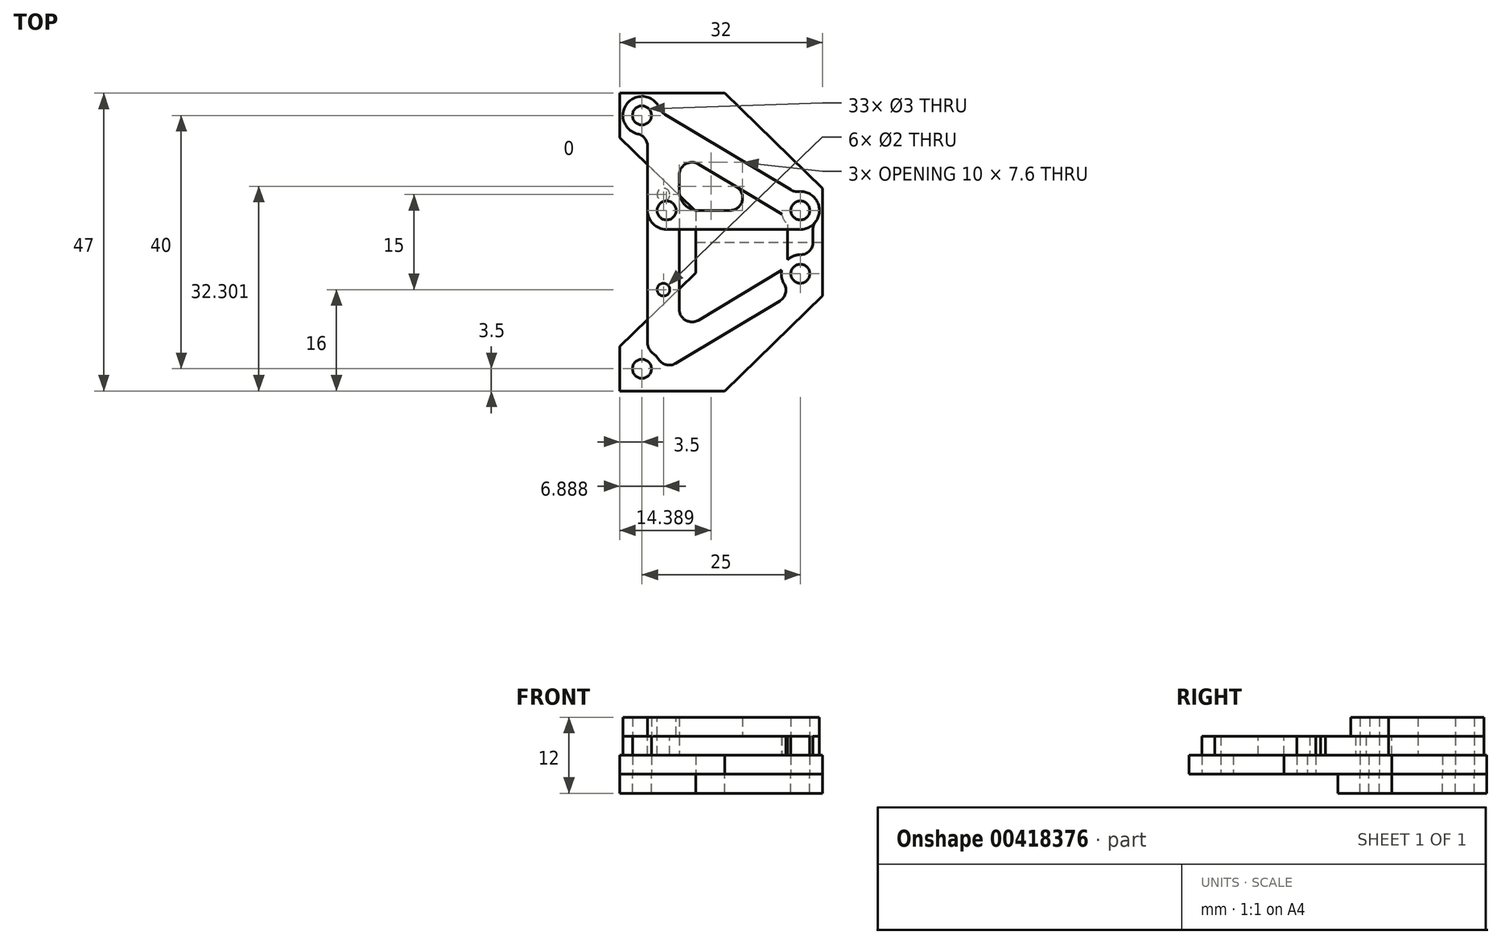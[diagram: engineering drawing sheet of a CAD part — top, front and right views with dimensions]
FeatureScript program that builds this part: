
annotation { "Feature Type Name" : "Feature", "Feature Type Description" : "" }
export const myFeature = defineFeature(function(context is Context, id is Id, definition is map)
    precondition{}
    {
        {
            var Q0;
            Q0=qCreatedBy(makeId("Top.planeOp"),FACE);
            var sketch = newSketch(context, id + "F0", { "sketchPlane" : qUnion([Q0])});
            skCircle(sketch, "E0", {"center": v(0, 20) * mm, "radius": 1.5 * mm});
            skCircle(sketch, "E1", {"center": v(25, 5) * mm, "radius": 1.5 * mm});
            skCircle(sketch, "E2.MirrorC", {"center": v(0, -20) * mm, "radius": 1.5 * mm});
            skCircle(sketch, "E3.MirrorC", {"center": v(25, -5) * mm, "radius": 1.5 * mm});
            skLineSegment(sketch, "E4", {"start": v(8.5, 4.85) * mm, "end": v(-3.5, 16.5) * mm});
            skLineSegment(sketch, "E5", {"start": v(-3.5, 16.5) * mm, "end": v(-3.5, 23.5) * mm});
            skLineSegment(sketch, "E6", {"start": v(-3.5, 23.5) * mm, "end": v(13.05, 23.5) * mm});
            skLineSegment(sketch, "E7", {"start": v(13.05, 23.5) * mm, "end": v(28.5, 8.5) * mm});
            skLineSegment(sketch, "E8", {"start": v(28.5, 8.5) * mm, "end": v(28.5, 0) * mm});
            skLineSegment(sketch, "E9.MirrorCS", {"start": v(8.5, -4.85) * mm, "end": v(-3.5, -16.5) * mm});
            skLineSegment(sketch, "E10.MirrorCS", {"start": v(-3.5, -16.5) * mm, "end": v(-3.5, -23.5) * mm});
            skLineSegment(sketch, "E11.MirrorCS", {"start": v(-3.5, -23.5) * mm, "end": v(13.05, -23.5) * mm});
            skLineSegment(sketch, "E12.MirrorCS", {"start": v(13.05, -23.5) * mm, "end": v(28.5, -8.5) * mm});
            skLineSegment(sketch, "E13.MirrorCS", {"start": v(28.5, -8.5) * mm, "end": v(28.5, 0) * mm});
            skLineSegment(sketch, "E14", {"start": v(8.5, 4.85) * mm, "end": v(8.5, -4.85) * mm});
            skPoint(sketch, "E15.orphan", {"position": v(13.5, 0) * mm});
            skLineSegment(sketch, "E16", {"start": v(8.5, 0) * mm, "end": v(28.5, 0) * mm});
            skSolve(sketch);
        }
        {
            var Q0;
            Q0 = qSketchRegion(id + "F0", true);
            extrude(context, id + "F1", {"entities" : qUnion([Q0]), "depth" : 3 * mm, "offsetDistance" : 25 * mm});
        }
        {
            var Q0;
            Q0=makeQuery(id+"F0.imprint","IMPRINT",FACE,{"disambiguationData":[TD([[makeQuery(id+"F0.imprint","IMPRINT",EDGE,{"derivedFrom":sQuery(id+"F0.wireOp",EDGE,"E0")}),-1.0]])]});
            extrude(context, id + "F2", {"entities" : qUnion([Q0]), "oppositeDirection" : true, "depth" : 3 * mm, "offsetDistance" : 25 * mm});
        }
        {
            var Q0;
            Q0=makeQuery(id+"F1.opExtrude","CAP_FACE",FACE,{"disambiguationData":[OSD([sQuery(id+"F0.wireOp",EDGE,"E0"),sQuery(id+"F0.wireOp",EDGE,"E1"),sQuery(id+"F0.wireOp",EDGE,"E2.MirrorC"),sQuery(id+"F0.wireOp",EDGE,"E3.MirrorC"),sQuery(id+"F0.wireOp",EDGE,"E4"),sQuery(id+"F0.wireOp",EDGE,"E5"),sQuery(id+"F0.wireOp",EDGE,"E6"),sQuery(id+"F0.wireOp",EDGE,"E7"),sQuery(id+"F0.wireOp",EDGE,"E8"),sQuery(id+"F0.wireOp",EDGE,"E9.MirrorCS"),sQuery(id+"F0.wireOp",EDGE,"E10.MirrorCS"),sQuery(id+"F0.wireOp",EDGE,"E11.MirrorCS"),sQuery(id+"F0.wireOp",EDGE,"E12.MirrorCS"),sQuery(id+"F0.wireOp",EDGE,"E13.MirrorCS"),sQuery(id+"F0.wireOp",EDGE,"E14")])],"isStart":false});
            var sketch = newSketch(context, id + "F3", { "sketchPlane" : qUnion([Q0])});
            skCircle(sketch, "E17.0", {"center": v(0, 20) * mm, "radius": 1.5 * mm});
            skCircle(sketch, "E18.0", {"center": v(25, 5) * mm, "radius": 1.5 * mm});
            skCircle(sketch, "E19", {"center": v(0, 20) * mm, "radius": 3 * mm});
            skCircle(sketch, "E20", {"center": v(25, 5) * mm, "radius": 3 * mm});
            skPoint(sketch, "E21", {"position": v(1.5, 20) * mm});
            skPoint(sketch, "E22", {"position": v(3, 20) * mm});
            skPoint(sketch, "E23", {"position": v(26.5, 5) * mm});
            skPoint(sketch, "E24", {"position": v(28, 5) * mm});
            skLineSegment(sketch, "E25", {"start": v(0, 20) * mm, "end": v(25, 5) * mm, "construction": true});
            skCircle(sketch, "E26.0", {"center": v(25, -5) * mm, "radius": 1.5 * mm});
            skLineSegment(sketch, "E27", {"start": v(25, 5) * mm, "end": v(25, -5) * mm, "construction": true});
            skCircle(sketch, "E28.MirrorC", {"center": v(25, -5) * mm, "radius": 3 * mm});
            skCircle(sketch, "E29.MirrorC", {"center": v(0, -20) * mm, "radius": 3 * mm});
            skLineSegment(sketch, "E30", {"start": v(23, 2.76) * mm, "end": v(23, -2.76) * mm});
            skLineSegment(sketch, "E31.MirrorCS", {"start": v(27, 2.76) * mm, "end": v(27, -2.76) * mm});
            skLineSegment(sketch, "E32", {"start": v(0.89, 17.13) * mm, "end": v(22.05, 4.44) * mm});
            skLineSegment(sketch, "E33.MirrorCS", {"start": v(2.95, 20.56) * mm, "end": v(24.11, 7.87) * mm});
            skLineSegment(sketch, "E34.MirrorCS", {"start": v(0.89, -17.13) * mm, "end": v(22.05, -4.44) * mm});
            skLineSegment(sketch, "E35.MirrorCS", {"start": v(2.95, -20.56) * mm, "end": v(24.11, -7.87) * mm});
            skLineSegment(sketch, "E36", {"start": v(0.89, 17.13) * mm, "end": v(0.89, -17.13) * mm});
            skLineSegment(sketch, "E37", {"start": v(5.89, 14.13) * mm, "end": v(5.89, -14.13) * mm});
            skSolve(sketch);
        }
        {
            var Q0;
            Q0=makeQuery(id+"F3.imprint","IMPRINT",FACE,{"disambiguationData":[TD([[makeQuery(id+"F3.imprint","IMPRINT",EDGE,{"derivedFrom":sQuery(id+"F3.wireOp",EDGE,"E17.0")}),-1.0]])]});
            var Q1;
            Q1=makeQuery(id+"F3.imprint","IMPRINT",FACE,{"disambiguationData":[TD([[makeQuery(id+"F3.imprint","IMPRINT",EDGE,{"derivedFrom":makeQuery(id+"F1.opExtrude","CAP_EDGE",EDGE,{"disambiguationData":[OSD([sQuery(id+"F0.wireOp",EDGE,"E2.MirrorC")])],"isStart":false})}),1.0]])]});
            var Q2;
            {var subQ0=sQuery(id+"F3.wireOp",EDGE,"E30");Q2=makeQuery(id+"F3.imprint","IMPRINT",FACE,{"disambiguationData":[TD([[makeQuery(id+"F3.imprint","IMPRINT",EDGE,{"derivedFrom":subQ0}),1.0]])]});}
            var Q3;
            Q3=makeQuery(id+"F3.imprint","IMPRINT",FACE,{"disambiguationData":[TD([[makeQuery(id+"F3.imprint","IMPRINT",EDGE,{"derivedFrom":sQuery(id+"F3.wireOp",EDGE,"E18.0")}),-1.0]])]});
            var Q4;
            {var subQ6=sQuery(id+"F3.wireOp",EDGE,"E33.MirrorCS");Q4=makeQuery(id+"F3.imprint","IMPRINT",FACE,{"disambiguationData":[TD([[makeQuery(id+"F3.imprint","IMPRINT",EDGE,{"derivedFrom":subQ6}),-1.0]])]});}
            var Q5;
            Q5=makeQuery(id+"F3.imprint","IMPRINT",FACE,{"disambiguationData":[TD([[makeQuery(id+"F3.imprint","IMPRINT",EDGE,{"derivedFrom":sQuery(id+"F3.wireOp",EDGE,"E26.0")}),1.0]])]});
            var Q6;
            {var subQ6=sQuery(id+"F3.wireOp",EDGE,"E35.MirrorCS");Q6=makeQuery(id+"F3.imprint","IMPRINT",FACE,{"disambiguationData":[TD([[makeQuery(id+"F3.imprint","IMPRINT",EDGE,{"derivedFrom":subQ6}),1.0]])]});}
            var Q7;
            {var subQ1=sQuery(id+"F3.wireOp",EDGE,"E32");var subQ3=sQuery(id+"F3.wireOp",EDGE,"E37");var subQ4=makeQuery(id+"F3.imprint","INTERSECT",VERTEX,{"derivedFrom":[subQ1,subQ3]});Q7=makeQuery(id+"F3.imprint","IMPRINT",FACE,{"disambiguationData":[TD([[makeQuery(id+"F3.imprint","IMPRINT",EDGE,{"disambiguationData":[TD([[subQ4,-1.0]])],"derivedFrom":subQ3}),-1.0]])]});}
            var Q8;
            {var subQ1=sQuery(id+"F3.wireOp",EDGE,"E34.MirrorCS");var subQ3=sQuery(id+"F3.wireOp",EDGE,"E37");var subQ4=makeQuery(id+"F3.imprint","INTERSECT",VERTEX,{"derivedFrom":[subQ1,subQ3]});Q8=makeQuery(id+"F3.imprint","IMPRINT",FACE,{"disambiguationData":[TD([[makeQuery(id+"F3.imprint","IMPRINT",EDGE,{"disambiguationData":[TD([[subQ4,1.0]])],"derivedFrom":subQ3}),-1.0]])]});}
            var Q9;
            {var subQ0=sQuery(id+"F3.wireOp",EDGE,"E36");var subQ1=makeQuery(id+"F1.opExtrude","CAP_EDGE",EDGE,{"disambiguationData":[OSD([sQuery(id+"F0.wireOp",EDGE,"E4")])],"isStart":false});var subQ2=makeQuery(id+"F3.imprint","INTERSECT",VERTEX,{"derivedFrom":[subQ1,subQ0]});Q9=makeQuery(id+"F3.imprint","IMPRINT",FACE,{"disambiguationData":[TD([[makeQuery(id+"F3.imprint","IMPRINT",EDGE,{"disambiguationData":[TD([[subQ2,-1.0]])],"derivedFrom":subQ0}),1.0]])]});}
            extrude(context, id + "F4", {"entities" : qUnion([Q0, Q1, Q2, Q3, Q4, Q5, Q6, Q7, Q8, Q9]), "depth" : 3 * mm, "offsetDistance" : 25 * mm});
        }
        {
            var Q0;
            Q0=makeQuery(id+"F4.opExtrude","SWEPT_EDGE",EDGE,{"disambiguationData":[OSD([sQuery(id+"F3.wireOp",EDGE,"E19"),sQuery(id+"F3.wireOp",EDGE,"E32"),sQuery(id+"F3.wireOp",EDGE,"E36")])]});
            var Q1;
            Q1=makeQuery(id+"F4.opExtrude","SWEPT_EDGE",EDGE,{"disambiguationData":[OSD([sQuery(id+"F3.wireOp",EDGE,"E29.MirrorC"),sQuery(id+"F3.wireOp",EDGE,"E34.MirrorCS"),sQuery(id+"F3.wireOp",EDGE,"E36")])]});
            var Q2;
            Q2=makeQuery(id+"F4.opExtrude","SWEPT_EDGE",EDGE,{"disambiguationData":[OSD([sQuery(id+"F3.wireOp",EDGE,"E29.MirrorC"),sQuery(id+"F3.wireOp",EDGE,"E35.MirrorCS")])]});
            var Q3;
            Q3=makeQuery(id+"F4.opExtrude","SWEPT_EDGE",EDGE,{"disambiguationData":[OSD([sQuery(id+"F3.wireOp",EDGE,"E28.MirrorC"),sQuery(id+"F3.wireOp",EDGE,"E35.MirrorCS")])]});
            var Q4;
            Q4=makeQuery(id+"F4.opExtrude","SWEPT_EDGE",EDGE,{"disambiguationData":[OSD([sQuery(id+"F3.wireOp",EDGE,"E20"),sQuery(id+"F3.wireOp",EDGE,"E31.MirrorCS")])]});
            var Q5;
            Q5=makeQuery(id+"F4.opExtrude","SWEPT_EDGE",EDGE,{"disambiguationData":[OSD([sQuery(id+"F3.wireOp",EDGE,"E28.MirrorC"),sQuery(id+"F3.wireOp",EDGE,"E31.MirrorCS")])]});
            var Q6;
            Q6=makeQuery(id+"F4.opExtrude","SWEPT_EDGE",EDGE,{"disambiguationData":[OSD([sQuery(id+"F3.wireOp",EDGE,"E20"),sQuery(id+"F3.wireOp",EDGE,"E33.MirrorCS")])]});
            var Q7;
            Q7=makeQuery(id+"F4.opExtrude","SWEPT_EDGE",EDGE,{"disambiguationData":[OSD([sQuery(id+"F3.wireOp",EDGE,"E34.MirrorCS"),sQuery(id+"F3.wireOp",EDGE,"E37")])]});
            var Q8;
            Q8=makeQuery(id+"F4.opExtrude","SWEPT_EDGE",EDGE,{"disambiguationData":[OSD([sQuery(id+"F3.wireOp",EDGE,"E32"),sQuery(id+"F3.wireOp",EDGE,"E37")])]});
            var Q9;
            Q9=makeQuery(id+"F4.opExtrude","SWEPT_EDGE",EDGE,{"disambiguationData":[OSD([sQuery(id+"F3.wireOp",EDGE,"E19"),sQuery(id+"F3.wireOp",EDGE,"E33.MirrorCS")])]});
            fillet(context, id + "F5", {"entities" : qUnion([Q0, Q1, Q2, Q3, Q4, Q5, Q6, Q7, Q8, Q9]), "radius" : 2 * mm, "tangentPropagation" : true, "allowEdgeOverflow" : false});
        }
        {
            var Q0;
            Q0=makeQuery(id+"F4.opExtrude","CAP_FACE",FACE,{"disambiguationData":[OSD([sQuery(id+"F0.wireOp",EDGE,"E2.MirrorC"),sQuery(id+"F3.wireOp",EDGE,"E17.0"),sQuery(id+"F3.wireOp",EDGE,"E18.0"),sQuery(id+"F3.wireOp",EDGE,"E19"),sQuery(id+"F3.wireOp",EDGE,"E20"),sQuery(id+"F3.wireOp",EDGE,"E26.0"),sQuery(id+"F3.wireOp",EDGE,"E28.MirrorC"),sQuery(id+"F3.wireOp",EDGE,"E29.MirrorC"),sQuery(id+"F3.wireOp",EDGE,"E30"),sQuery(id+"F3.wireOp",EDGE,"E31.MirrorCS"),sQuery(id+"F3.wireOp",EDGE,"E32"),sQuery(id+"F3.wireOp",EDGE,"E33.MirrorCS"),sQuery(id+"F3.wireOp",EDGE,"E34.MirrorCS"),sQuery(id+"F3.wireOp",EDGE,"E35.MirrorCS"),sQuery(id+"F3.wireOp",EDGE,"E36"),sQuery(id+"F3.wireOp",EDGE,"E37")])],"isStart":false});
            var sketch = newSketch(context, id + "F6", { "sketchPlane" : qUnion([Q0])});
            skCircle(sketch, "E38.0", {"center": v(0, 20) * mm, "radius": 3 * mm});
            skCircle(sketch, "E39.0", {"center": v(0, 20) * mm, "radius": 1.5 * mm});
            skCircle(sketch, "E40.0", {"center": v(25, 5) * mm, "radius": 1.5 * mm});
            skCircle(sketch, "E41.0", {"center": v(25, 5) * mm, "radius": 3 * mm});
            skArc(sketch, "E42.0", {"start": v(3.6, 20.17) * mm, "mid": v(3.11, 20.58) * mm, "end": v(2.78, 21.13) * mm});
            skLineSegment(sketch, "E43.0", {"start": v(2.95, 20.56) * mm, "end": v(24.11, 7.87) * mm});
            skArc(sketch, "E44.0", {"start": v(24.7, 7.98) * mm, "mid": v(24.05, 8.02) * mm, "end": v(23.46, 8.26) * mm});
            skArc(sketch, "E45.0", {"start": v(-0.67, 17.08) * mm, "mid": v(0.45, 16.37) * mm, "end": v(0.89, 15.13) * mm});
            skLineSegment(sketch, "E46.0", {"start": v(0.89, 17.13) * mm, "end": v(0.89, 2) * mm});
            skArc(sketch, "E47.0", {"start": v(5.89, 10.6) * mm, "mid": v(6.9, 12.34) * mm, "end": v(8.92, 12.32) * mm});
            skLineSegment(sketch, "E48.0", {"start": v(5.89, 14.13) * mm, "end": v(5.89, 2) * mm});
            skLineSegment(sketch, "E49.0", {"start": v(0.89, 17.13) * mm, "end": v(14.92, 8.71) * mm});
            skLineSegment(sketch, "E50", {"start": v(25, 2) * mm, "end": v(5.89, 2) * mm});
            skLineSegment(sketch, "E51", {"start": v(5.89, 5) * mm, "end": v(13.9, 5) * mm});
            skLineSegment(sketch, "E52", {"start": v(5.89, 2) * mm, "end": v(0.89, 2) * mm});
            skPoint(sketch, "E53.orphan", {"position": v(0.89, -17.13) * mm});
            skPoint(sketch, "E54.orphan", {"position": v(5.89, -14.13) * mm});
            skPoint(sketch, "E55.newPointA", {"position": v(22.05, 4.44) * mm});
            skArc(sketch, "E55.filletArc", {"start": v(13.9, 5) * mm, "mid": v(15.82, 6.47) * mm, "end": v(14.92, 8.71) * mm});
            skSolve(sketch);
        }
        {
            var Q0;
            Q0 = qSketchRegion(id + "F6", true);
            var Q1;
            {var subQ0=sQuery(id+"F6.wireOp",EDGE,"E47.0");Q1=makeQuery(id+"F6.imprint","IMPRINT",FACE,{"disambiguationData":[TD([[makeQuery(id+"F6.imprint","IMPRINT",EDGE,{"derivedFrom":subQ0}),1.0]])]});}
            extrude(context, id + "F7", {"entities" : qUnion([Q0, Q1]), "depth" : 3 * mm, "offsetDistance" : 25 * mm});
        }
        {
            var Q0;
            Q0=makeQuery(id+"F7.opExtrude","SWEPT_EDGE",EDGE,{"disambiguationData":[OSD([sQuery(id+"F6.wireOp",EDGE,"E48.0"),sQuery(id+"F6.wireOp",EDGE,"E51")])]});
            var Q1;
            Q1=makeQuery(id+"F7.opExtrude","SWEPT_EDGE",EDGE,{"disambiguationData":[OSD([sQuery(id+"F3.wireOp",EDGE,"E36"),sQuery(id+"F6.wireOp",EDGE,"E46.0"),sQuery(id+"F6.wireOp",EDGE,"E52")])]});
            fillet(context, id + "F8", {"entities" : qUnion([Q0, Q1]), "radius" : 3 * mm, "tangentPropagation" : true, "allowEdgeOverflow" : false});
        }
        {
            var Q0;
            Q0=makeQuery(id+"F4.opExtrude","CAP_FACE",FACE,{"disambiguationData":[OSD([sQuery(id+"F0.wireOp",EDGE,"E2.MirrorC"),sQuery(id+"F3.wireOp",EDGE,"E17.0"),sQuery(id+"F3.wireOp",EDGE,"E18.0"),sQuery(id+"F3.wireOp",EDGE,"E19"),sQuery(id+"F3.wireOp",EDGE,"E20"),sQuery(id+"F3.wireOp",EDGE,"E26.0"),sQuery(id+"F3.wireOp",EDGE,"E28.MirrorC"),sQuery(id+"F3.wireOp",EDGE,"E29.MirrorC"),sQuery(id+"F3.wireOp",EDGE,"E30"),sQuery(id+"F3.wireOp",EDGE,"E31.MirrorCS"),sQuery(id+"F3.wireOp",EDGE,"E32"),sQuery(id+"F3.wireOp",EDGE,"E33.MirrorCS"),sQuery(id+"F3.wireOp",EDGE,"E34.MirrorCS"),sQuery(id+"F3.wireOp",EDGE,"E35.MirrorCS"),sQuery(id+"F3.wireOp",EDGE,"E36"),sQuery(id+"F3.wireOp",EDGE,"E37")])],"isStart":false});
            var sketch = newSketch(context, id + "F9", { "sketchPlane" : qUnion([Q0])});
            skLineSegment(sketch, "E56", {"start": v(5.89, 0) * mm, "end": v(0.89, 0) * mm, "construction": true});
            skLineSegment(sketch, "E57", {"start": v(3.39, 0) * mm, "end": v(3.39, 15.13) * mm, "construction": true});
            skCircle(sketch, "E58", {"center": v(3.39, 7.5) * mm, "radius": 1 * mm});
            skCircle(sketch, "E59.MirrorC", {"center": v(3.39, -7.5) * mm, "radius": 1 * mm});
            skSolve(sketch);
        }
        {
            var Q0;
            Q0 = qSketchRegion(id + "F9", true);
            extrude(context, id + "F10", {"entities" : qUnion([Q0]), "operationType" : NewBodyOperationType.REMOVE, "endBound" : BoundingType.UP_TO_NEXT, "oppositeDirection" : true, "depth" : 25 * mm, "offsetDistance" : 25 * mm});
        }
        {
            var Q0;
            Q0=makeQuery(id+"F7.opExtrude","CAP_FACE",FACE,{"disambiguationData":[OSD([sQuery(id+"F6.wireOp",EDGE,"E38.0"),sQuery(id+"F6.wireOp",EDGE,"E39.0"),sQuery(id+"F6.wireOp",EDGE,"E40.0"),sQuery(id+"F6.wireOp",EDGE,"E41.0"),sQuery(id+"F6.wireOp",EDGE,"E42.0"),sQuery(id+"F6.wireOp",EDGE,"E43.0"),sQuery(id+"F6.wireOp",EDGE,"E44.0"),sQuery(id+"F6.wireOp",EDGE,"E45.0"),sQuery(id+"F6.wireOp",EDGE,"E46.0"),sQuery(id+"F6.wireOp",EDGE,"E47.0"),sQuery(id+"F6.wireOp",EDGE,"E48.0"),sQuery(id+"F6.wireOp",EDGE,"E49.0"),sQuery(id+"F6.wireOp",EDGE,"E50"),sQuery(id+"F6.wireOp",EDGE,"E51"),sQuery(id+"F6.wireOp",EDGE,"E52"),sQuery(id+"F6.wireOp",EDGE,"E55.filletArc")])],"isStart":false});
            var sketch = newSketch(context, id + "F11", { "sketchPlane" : qUnion([Q0])});
            skArc(sketch, "E60.0", {"start": v(0.89, 5) * mm, "mid": v(1.77, 2.88) * mm, "end": v(3.89, 2) * mm, "construction": true});
            skCircle(sketch, "E61", {"center": v(3.89, 5) * mm, "radius": 1.5 * mm});
            skSolve(sketch);
        }
        {
            var Q0;
            Q0 = qSketchRegion(id + "F11", true);
            extrude(context, id + "F12", {"entities" : qUnion([Q0]), "operationType" : NewBodyOperationType.REMOVE, "endBound" : BoundingType.UP_TO_NEXT, "oppositeDirection" : true, "depth" : 25 * mm, "offsetDistance" : 25 * mm});
        }
    });
